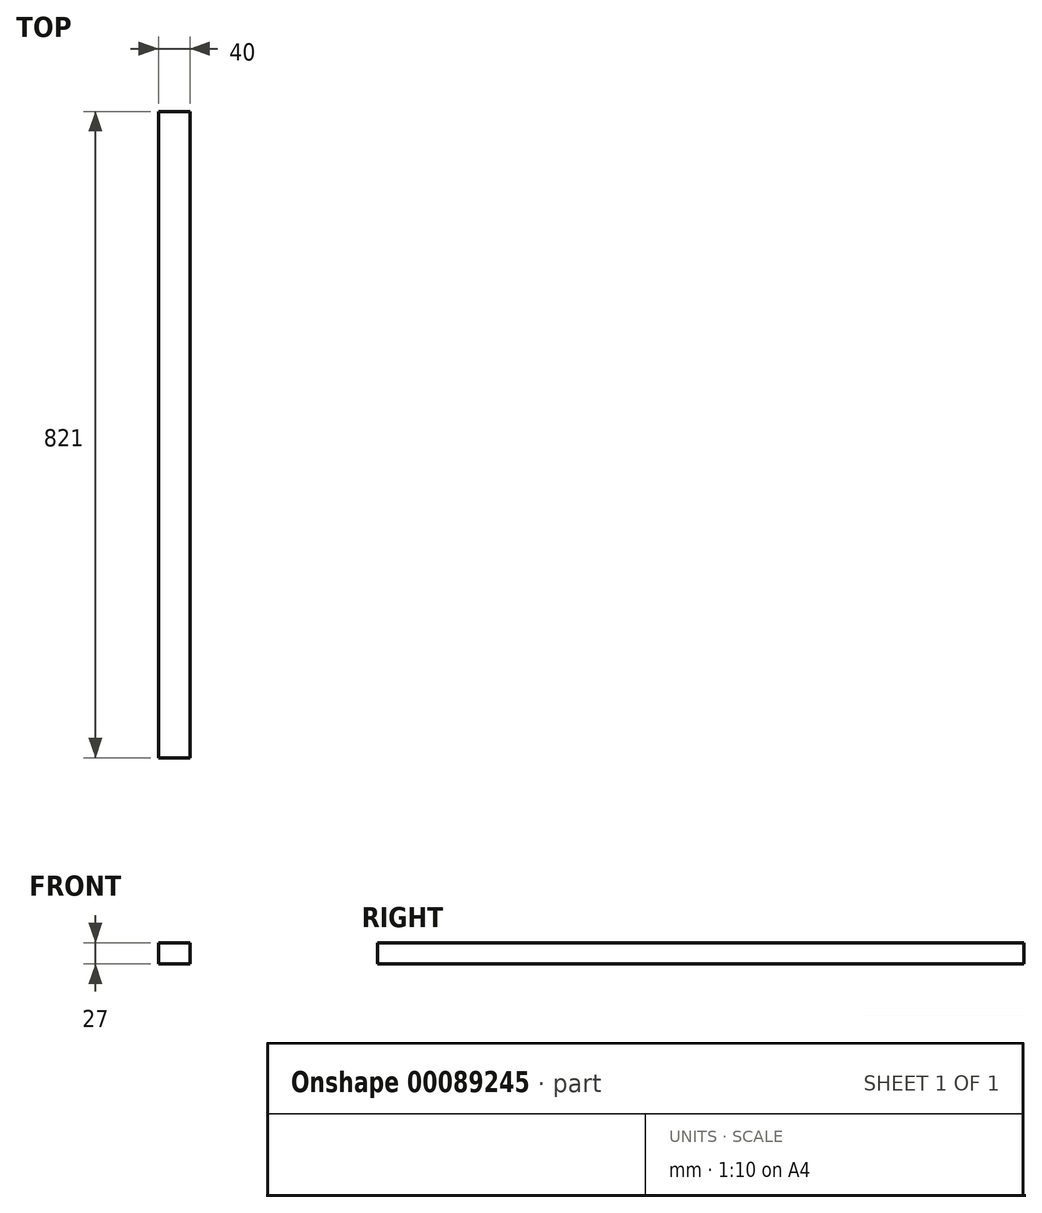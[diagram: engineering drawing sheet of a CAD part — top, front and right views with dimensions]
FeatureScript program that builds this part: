
annotation { "Feature Type Name" : "Feature", "Feature Type Description" : "" }
export const myFeature = defineFeature(function(context is Context, id is Id, definition is map)
    precondition{}
    {
        {
            var Q0;
            Q0=qCreatedBy(makeId("Front.planeOp"),FACE);
            var sketch = newSketch(context, id + "F0", { "sketchPlane" : qUnion([Q0])});
            skLineSegment(sketch, "E0.bottom", {"start": v(-20, 13.5) * mm, "end": v(20, 13.5) * mm});
            skLineSegment(sketch, "E0.top", {"start": v(-20, -13.5) * mm, "end": v(20, -13.5) * mm});
            skLineSegment(sketch, "E0.left", {"start": v(-20, 13.5) * mm, "end": v(-20, -13.5) * mm});
            skLineSegment(sketch, "E0.right", {"start": v(20, 13.5) * mm, "end": v(20, -13.5) * mm});
            skPoint(sketch, "E0.middle", {"position": v(0, 0) * mm});
            skSolve(sketch);
        }
        {
            var Q0;
            Q0=makeQuery(id+"F0.imprint","IMPRINT",FACE,{"disambiguationData":[TD([[makeQuery(id+"F0.imprint","IMPRINT",EDGE,{"derivedFrom":sQuery(id+"F0.wireOp",EDGE,"E0.bottom")}),-1.0]])]});
            extrude(context, id + "F1", {"entities" : qUnion([Q0]), "depth" : 821 * mm});
        }
    });
